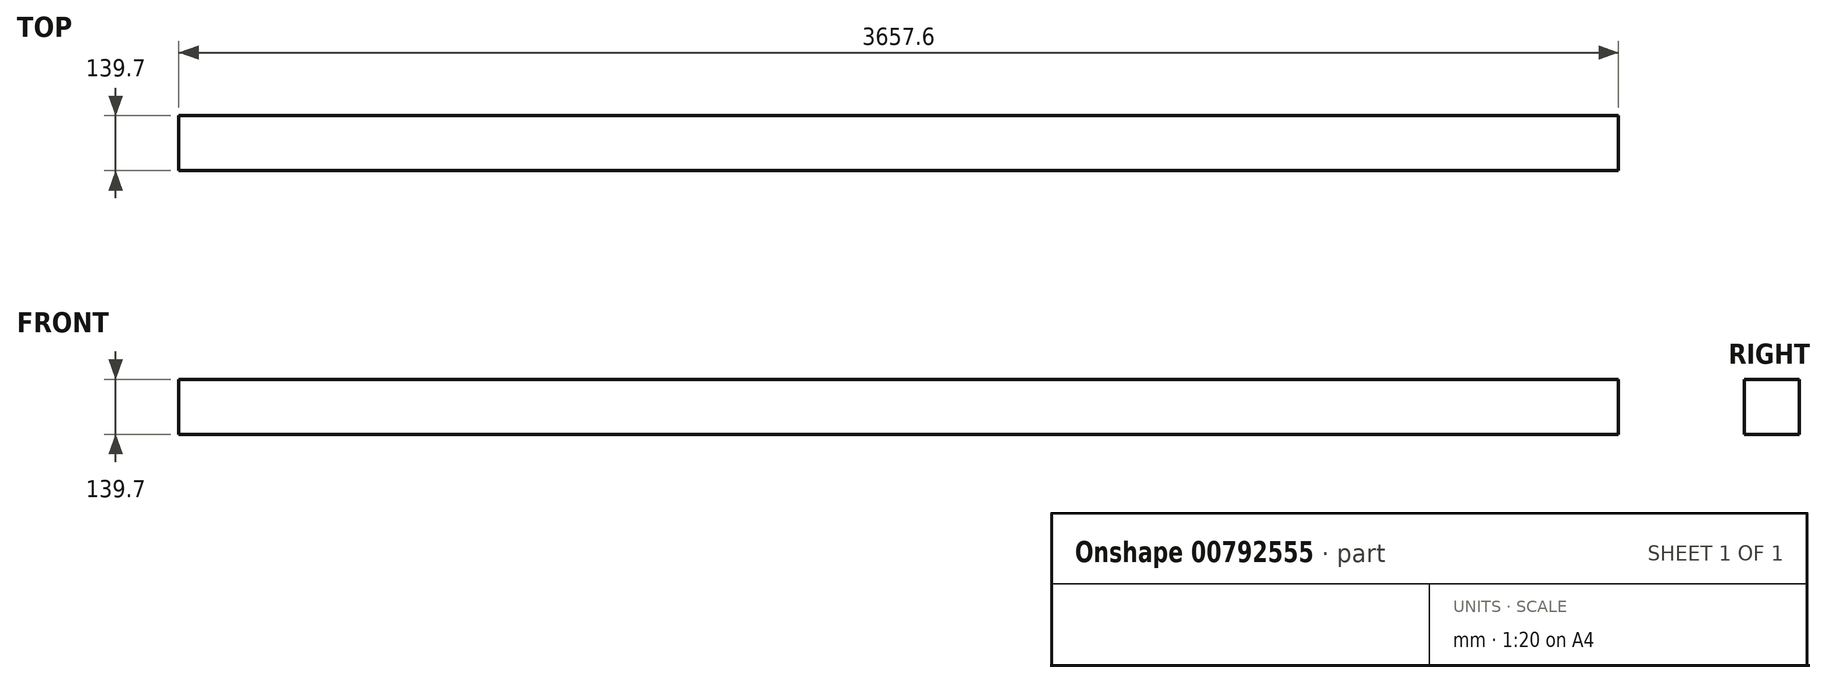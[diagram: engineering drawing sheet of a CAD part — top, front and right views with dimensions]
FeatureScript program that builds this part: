
annotation { "Feature Type Name" : "Feature", "Feature Type Description" : "" }
export const myFeature = defineFeature(function(context is Context, id is Id, definition is map)
    precondition{}
    {
        {
            var Q0;
            Q0=qCreatedBy(makeId("Right.planeOp"),FACE);
            var sketch = newSketch(context, id + "F0", { "sketchPlane" : qUnion([Q0])});
            skLineSegment(sketch, "E0.bottom", {"start": v(69.85, 69.85) * mm, "end": v(-69.85, 69.85) * mm});
            skLineSegment(sketch, "E0.top", {"start": v(69.85, -69.85) * mm, "end": v(-69.85, -69.85) * mm});
            skLineSegment(sketch, "E0.left", {"start": v(69.85, 69.85) * mm, "end": v(69.85, -69.85) * mm});
            skLineSegment(sketch, "E0.right", {"start": v(-69.85, 69.85) * mm, "end": v(-69.85, -69.85) * mm});
            skPoint(sketch, "E0.middle", {"position": v(0, 0) * mm});
            skSolve(sketch);
        }
        {
            var Q0;
            Q0 = qSketchRegion(id + "F0", true);
            extrude(context, id + "F1", {"entities" : qUnion([Q0]), "endBound" : BoundingType.SYMMETRIC, "depth" : 3657.6 * mm, "offsetDistance" : 25.4 * mm});
        }
    });
